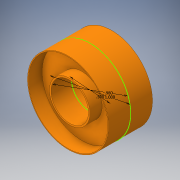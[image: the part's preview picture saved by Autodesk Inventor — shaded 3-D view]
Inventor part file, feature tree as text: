
AUTODESK INVENTOR PART (.ipt)
format: ipt  version: 2016 (Build 200138000, 138)  size: 131,072 bytes
history: native  units: in
note: dims shown in document units (in); Inventor stores cm internally (conversion verified against a paired STEP export)
features: extrude x4, fillet x2, sketch x1
ambient origin geometry x8: Origin, YZ Plane, XZ Plane, XY Plane, X Axis, Y Axis, Z Axis, Center Point
bodies: Solid1 (feature_tree)
feature tree (7):
  sketch  "Sketch1"  dims[d1=1.0in d2=0.98in d3=0.5in d4=0.24in d5=0.24in d6=0.0in d7=0.0in d8=0.27in d9=0.27in d10=0.0in d11=0.0in d12=0.1in d13=0.1in d14=0.0in d15=0.0in d16=0.25in d17=0.25in d18=0.0in d19=0.0in d20=0.001in d21=0.001in]
  extrude  "Extrusion1"  Depth=0.25in
  extrude  "Extrusion2"  Depth=0.5in
  extrude  "Extrusion3"  Depth=0.25in TaperAngle=0.0deg
  extrude  "Extrusion4"  Depth=0.27in TaperAngle=0.0deg
  fillet  "Fillet1"  Radius=0.1in
  fillet  "Fillet2"  Radius=0.25in
